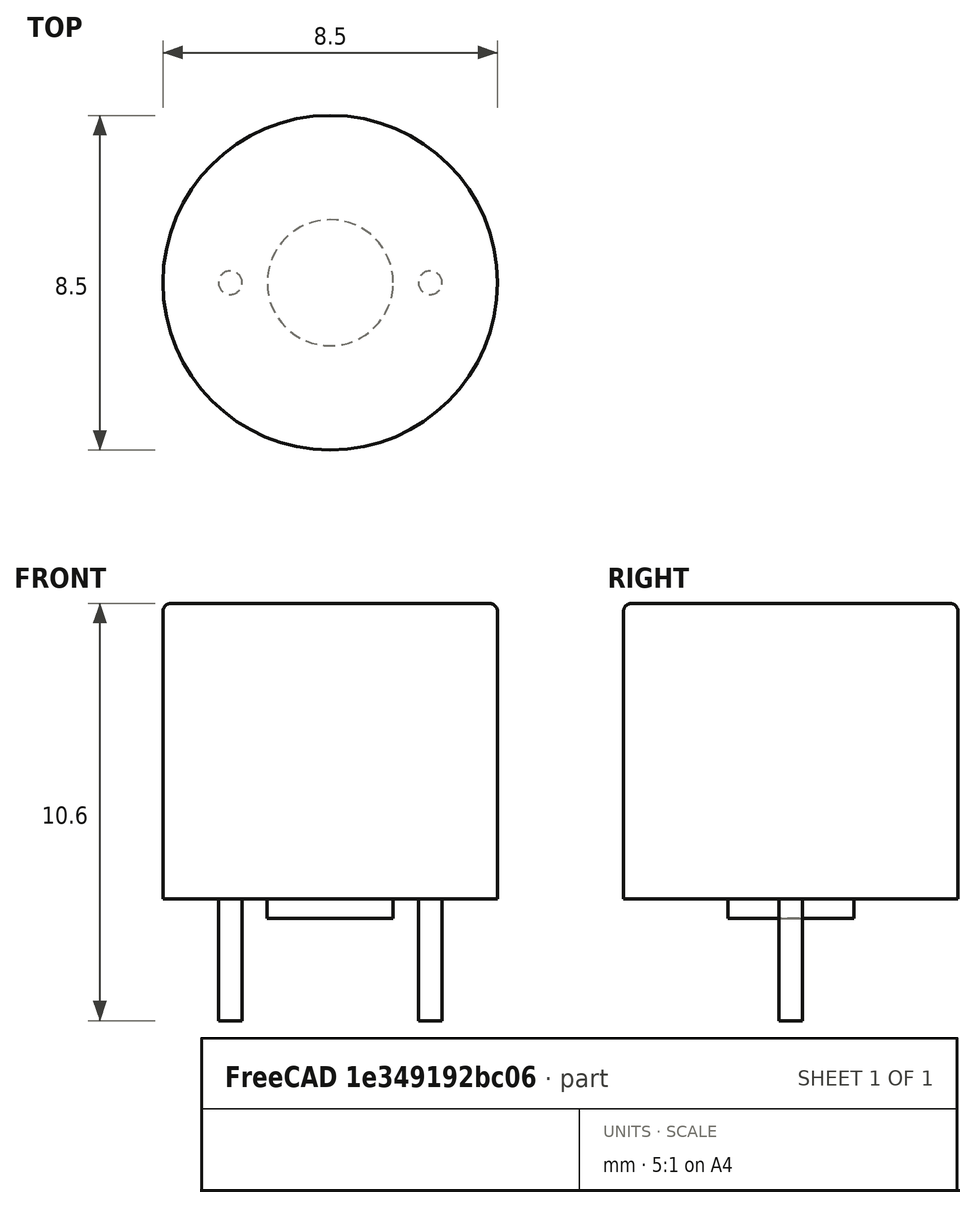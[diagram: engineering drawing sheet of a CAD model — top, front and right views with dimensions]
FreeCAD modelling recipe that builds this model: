
FCSTD DOCUMENT
Label: FUSE_TR5
objects: Part::Cylinder×4, Part::Fuse×1, Part::Fillet×1, Part::MultiFuse×1
note: 7 computed .brp shape members not serialized (recipe doc carries the construction recipe); baked Part::Feature solids carry a one-line shape summary decoded from their .brp

FEATURE [Part::Cylinder] Cylinder  label="Koerper"
  Angle = 360
  Height = 7.5
  Placement = pos=(0,0,0.5) rot=(0,0,1;0rad)
  Radius = 4.25
FEATURE [Part::Cylinder] Cylinder001  label="Fuss"
  Angle = 360
  Height = 0.5
  Radius = 1.6
FEATURE [Part::Fuse] Fusion
  Base = -> Cylinder
  Tool = -> Cylinder001
FEATURE [Part::Fillet] Fillet
  Base = -> Fusion
  Edges = 1 edges r=0.2: [Edge1]
FEATURE [Part::Cylinder] Cylinder002  label="pin1"
  Angle = 360
  Height = 3.1
  Placement = pos=(-2.54,0,-2.6) rot=(0,0,1;0rad)
  Radius = 0.3
FEATURE [Part::Cylinder] Cylinder003  label="pin2"
  Angle = 360
  Height = 3.1
  Placement = pos=(2.54,0,-2.6) rot=(0,0,1;0rad)
  Radius = 0.3
FEATURE [Part::MultiFuse] Fusion001  label="Fuse_TR5"
  Shapes = -> [Fillet,Cylinder002,Cylinder003]
